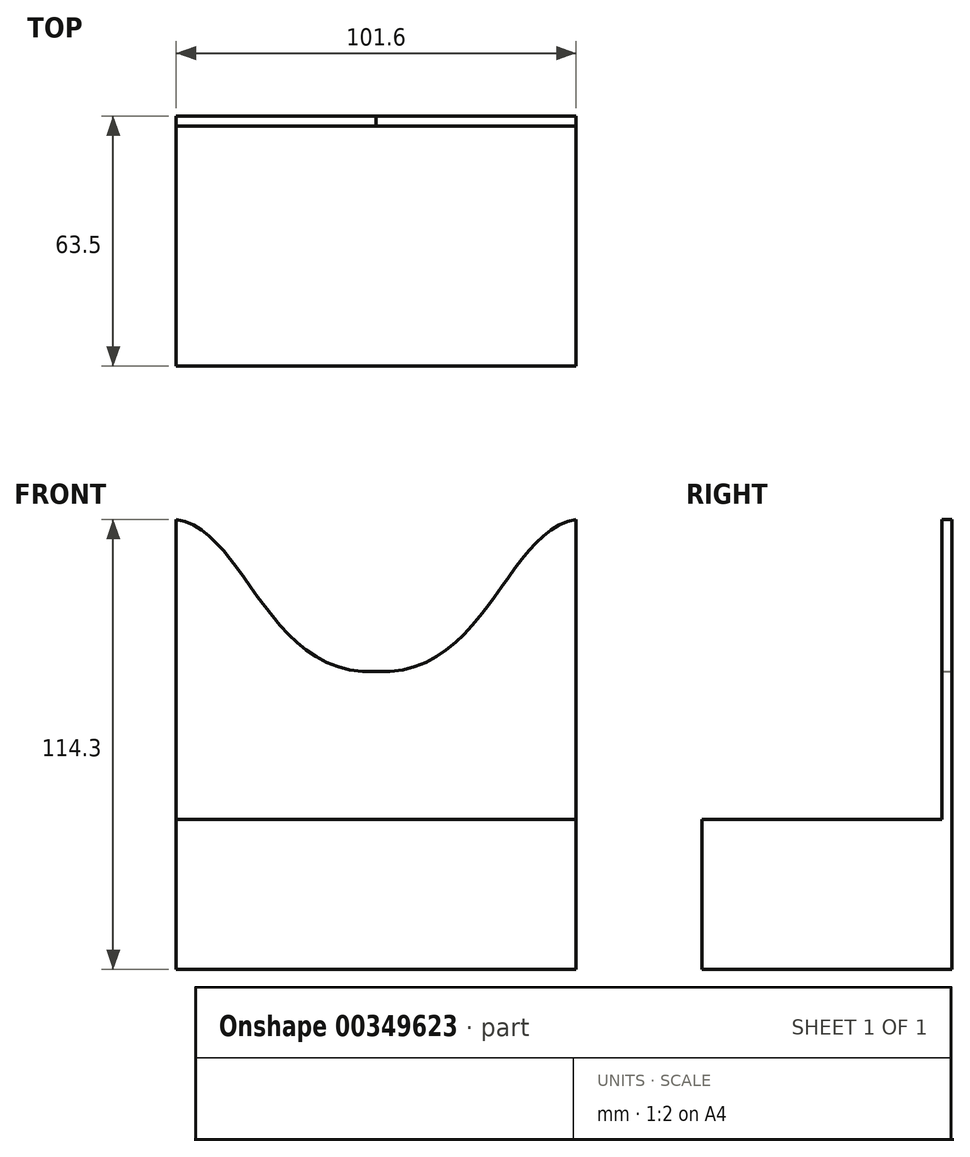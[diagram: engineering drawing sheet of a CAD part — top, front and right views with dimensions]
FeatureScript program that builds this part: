
annotation { "Feature Type Name" : "Feature", "Feature Type Description" : "" }
export const myFeature = defineFeature(function(context is Context, id is Id, definition is map)
    precondition{}
    {
        {
            var Q0;
            Q0=qCreatedBy(makeId("Front.planeOp"),FACE);
            var sketch = newSketch(context, id + "F0", { "sketchPlane" : qUnion([Q0])});
            skLineSegment(sketch, "E0.bottom", {"start": v(-101.6, 57.15) * mm, "end": v(-50.8, 57.15) * mm});
            skLineSegment(sketch, "E0.top", {"start": v(-101.6, -57.15) * mm, "end": v(101.6, -57.15) * mm});
            skLineSegment(sketch, "E0.left", {"start": v(-101.6, 57.15) * mm, "end": v(-101.6, -57.15) * mm});
            skLineSegment(sketch, "E0.right", {"start": v(101.6, 57.15) * mm, "end": v(101.6, -57.15) * mm});
            skPoint(sketch, "E0.middle", {"position": v(0, 0) * mm});
            skLineSegment(sketch, "E1", {"start": v(-50.8, 57.15) * mm, "end": v(-50.8, -57.15) * mm});
            skLineSegment(sketch, "E2", {"start": v(50.8, 57.15) * mm, "end": v(50.8, -57.15) * mm});
            skLineSegment(sketch, "E3", {"start": v(-50.8, -19.05) * mm, "end": v(50.8, -19.05) * mm});
            skFitSpline(sketch, "E4", {"points": [v(-50.8, 57.15) * mm, v(0, 18.54) * mm], "startDerivative": vector(53.36, -7.97) * mm, "endDerivative": vector(83.52, 4.56) * mm});
            skFitSpline(sketch, "E5.MirrorCS", {"points": [v(50.8, 57.15) * mm, v(0, 18.54) * mm], "startDerivative": vector(-53.36, -7.97) * mm, "endDerivative": vector(-83.52, 4.56) * mm});
            skLineSegment(sketch, "E6.trimOffspring", {"start": v(50.8, 57.15) * mm, "end": v(101.6, 57.15) * mm});
            skSolve(sketch);
        }
        {
            var Q0;
            {var subQ5=sQuery(id+"F0.wireOp",EDGE,"E3");Q0=makeQuery(id+"F0.imprint","IMPRINT",FACE,{"disambiguationData":[TD([[makeQuery(id+"F0.imprint","IMPRINT",EDGE,{"derivedFrom":subQ5}),-1.0]])]});}
            extrude(context, id + "F1", {"entities" : qUnion([Q0]), "depth" : 63.5 * mm});
        }
        {
            var Q0;
            {var subQ0=sQuery(id+"F0.wireOp",EDGE,"E3");Q0=makeQuery(id+"F0.imprint","IMPRINT",FACE,{"disambiguationData":[TD([[makeQuery(id+"F0.imprint","IMPRINT",EDGE,{"derivedFrom":subQ0}),1.0]])]});}
            extrude(context, id + "F2", {"entities" : qUnion([Q0]), "operationType" : NewBodyOperationType.ADD, "depth" : 2.54 * mm});
        }
    });
